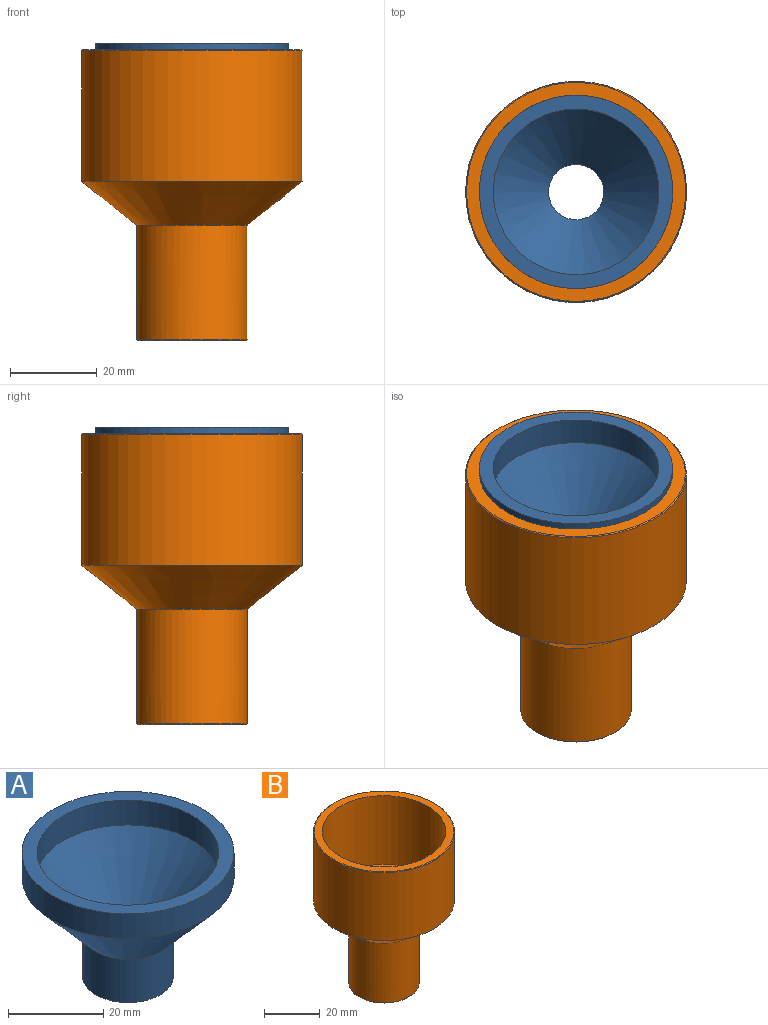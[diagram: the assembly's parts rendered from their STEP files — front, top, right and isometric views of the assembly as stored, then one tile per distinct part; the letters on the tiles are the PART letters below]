
ASSEMBLY  parts=2 mates=1
PART A: 8 faces, bbox 44.5x44.5x31.8 mm
  f0: cylinder r=19.05mm len=38.1mm, axis (0,0,-1), area 760.1mm2, adj f1,f7
  f1: cone r=19.05mm half-angle=41.6deg, axis (0,0,1), area 1527.1mm2, adj f0,f2
  f2: cylinder r=6.35mm len=12.7mm, axis (0,0,-1), area 442.2mm2, adj f1,f3
  f3: plane 19.05x19.05mm, normal (0,0,-1), area 158.3mm2, adj f2,f4
  f4: cylinder r=9.53mm len=19.05mm, axis (0,0,-1), area 663.3mm2, adj f3,f5
  f5: cone r=22.23mm half-angle=41.6deg, axis (0,0,1), area 1908.9mm2, adj f4,f6
  f6: cylinder r=22.23mm len=44.45mm, axis (0,0,-1), area 886.7mm2, adj f5,f7
  f7: plane 44.45x44.45mm, normal (0,0,1), area 411.7mm2, adj f0,f6
PART B: 10 faces, bbox 50.8x50.8x66.9 mm
  f0: cylinder r=22.23mm len=44.45mm, axis (0,0,-1), area 4225mm2, adj f1,f7
  f1: cone r=22.23mm half-angle=51.5deg, axis (0,0,1), area 1617.6mm2, adj f0,f2
  f2: cylinder r=9.53mm len=26.52mm, axis (0,0,-1), area 1587.2mm2, adj f1,f3
  f3: plane 24.94x24.94mm, normal (0,0,-1), area 203.6mm2, adj f2,f9
  f4: cylinder r=12.7mm len=26.29mm, axis (0,0,-1), area 2098mm2, adj f5,f9
  f5: cone r=25.4mm half-angle=51.5deg, axis (0,0,1), area 1941.1mm2, adj f4,f6
  f6: cylinder r=25.4mm len=50.8mm, axis (0,0,-1), area 4792.1mm2, adj f5,f8
  f7: plane 50.34x50.34mm, normal (0,0,1), area 438.7mm2, adj f0,f8
  f8: cone r=25.4mm half-angle=45deg, axis (0,0,-1), area 51.4mm2, adj f6,f7
  f9: cone r=12.47mm half-angle=45deg, axis (0,0,1), area 25.6mm2, adj f3,f4
PLACE A rot(axis=(0,0,-1),110.6deg) t=(-73.73,-20.43,-12.72)mm
PLACE B t=(-73.73,-20.43,-38.12)mm fixed
MATE revolute A.f0 <-> B.f0  axis (0,0,-1) through (-73.73,-20.43,-38.12)mm
